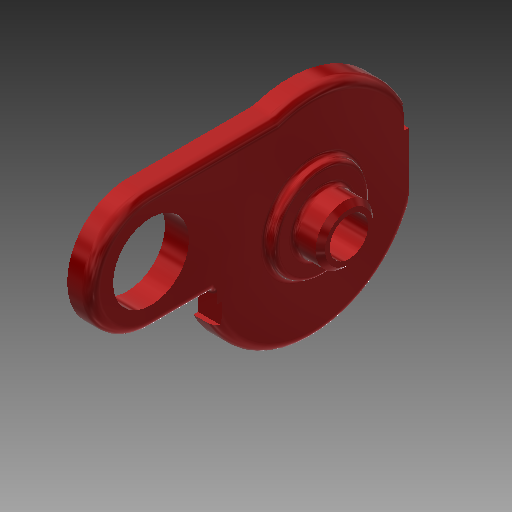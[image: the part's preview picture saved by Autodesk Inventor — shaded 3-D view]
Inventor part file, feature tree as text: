
AUTODESK INVENTOR PART (.ipt)
format: ipt  version: 2019 (Build 230136000, 136)  size: 357,376 bytes
history: native  units: in
note: dims shown in document units (in); Inventor stores cm internally (conversion verified against a paired STEP export)
features: sketch x4, other x2
ambient origin geometry x8: Origin, YZ Plane, XZ Plane, XY Plane, X Axis, Y Axis, Z Axis, Center Point
bodies: Solid1 (feature_tree)
feature tree (6):
  other  "Motor Endcap L.ipt"
  sketch  "Sketch1"  dims[d0=0.3937in]
  sketch  "Sketch2"
  sketch  "Sketch3"
  sketch  "Sketch4"
  other  "Solid1::Motor Endcap L.ipt"
